# Revit family: Cumberland-Sloane-Lounge
name_source: partatom
category: Furniture
revit_build: Autodesk Revit 2014 (Build: 20130308_1515(x64)
units: mm (PartAtom-declared; Revit-internal decimal feet)

## types (3) — shared parameters
Arm Finish = CUM - Linen - Beige
Assembly Code = E2020200
Back Finish = CUM - Linen - Beige
Depth = 28 9/16"
Height = 31 5/16"
Keynote = 12500
Leg Finish = CUM - UHMW, Black
Low Emitting Finish = Yes
Low Emitting Material = Yes
Manufacturer = Cumberland
Salvage or Reuse = Yes
Seat Finish = CUM - Linen - Beige
Type Comments = Sloane
URL = www.cumberlandfurniture.com
zero-valued in all types: Percentage of Recycled Content

## per-type parameters (varying)
| type | Cut | Cut Dist | D1 | D2 | Description | Leg C | Width |
| 2410 | No | 1/8" | 112 1/16" | 118 3/8" | Sloane 31"W 31"H 28"D | No | 31" |
| 2411 | Yes | 30" | 360" | 400" | Sloane 59"W 31"H 28"D | No | 59" |
| 2412 | Yes | 30" | 600" | 700" | Sloane 82"W 31"H 28"D | Yes | 82" |

note: column(s) folded — value = type name in every type: Model

## geometry (parser evidence)
native form markers: Sweep x7
no freeform markers — native parametric forms only
